# Revit family: Keilhauer-GSD-Bench-Corner-Low_Back-
name_source: partatom
category: Furniture
revit_build: Autodesk Revit 2016 (Build: 20150220_1215(x64)
units: mm (PartAtom-declared; Revit-internal decimal feet)

## family parameters
Always vertical = Yes
Cut with Voids When Loaded = No
OmniClass Number = 23.40.20.00
OmniClass Title = General Furniture and Specialties
Room Calculation Point = No
Shared = No
Work Plane-Based = No

## types (1)
- 88210
    Assembly Code = E2020200
    Depth = 26"
    Description = Low back corner
    Height = 36"
    Keynote = 12500
    Low Emitting Finish = Yes
    Low Emitting Material = Yes
    Manufacturer = Keilhauer
    Model = 88210
    Percentage of Recycled Content = 0
    Product Documentation Link = https://keilhauer.com
    Revit File Built By = https://servex-us.com
    Salvage or Reuse = Yes
    Type Comments = GSD
    URL = https://keilhauer.com
    Width = 26"

## geometry (parser evidence)
native form markers: Sweep x4
no freeform markers — native parametric forms only
